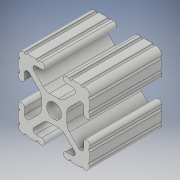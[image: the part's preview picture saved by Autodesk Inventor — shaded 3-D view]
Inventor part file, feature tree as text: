
AUTODESK INVENTOR PART (.ipt)
format: ipt  version: 2018 (Build 220112000, 112)  size: 209,920 bytes
history: native  units: in
note: dims shown in document units (in); Inventor stores cm internally (conversion verified against a paired STEP export)
features: extrude x1, sketch x1
ambient origin geometry x8: Origin, YZ Plane, XZ Plane, XY Plane, X Axis, Y Axis, Z Axis, Center Point
bodies: Solid1 (feature_tree)
feature tree (2):
  extrude  "Extrusion1"  [1 undecoded]
  sketch  "Sketch1"  dims[d0=1.0in d1=0.0in]
note: 1 required parameter value undecoded (feature->parameter linkage not recoverable at this tier; creation-order binding heuristic only, values carry confidence <= 0.55)
